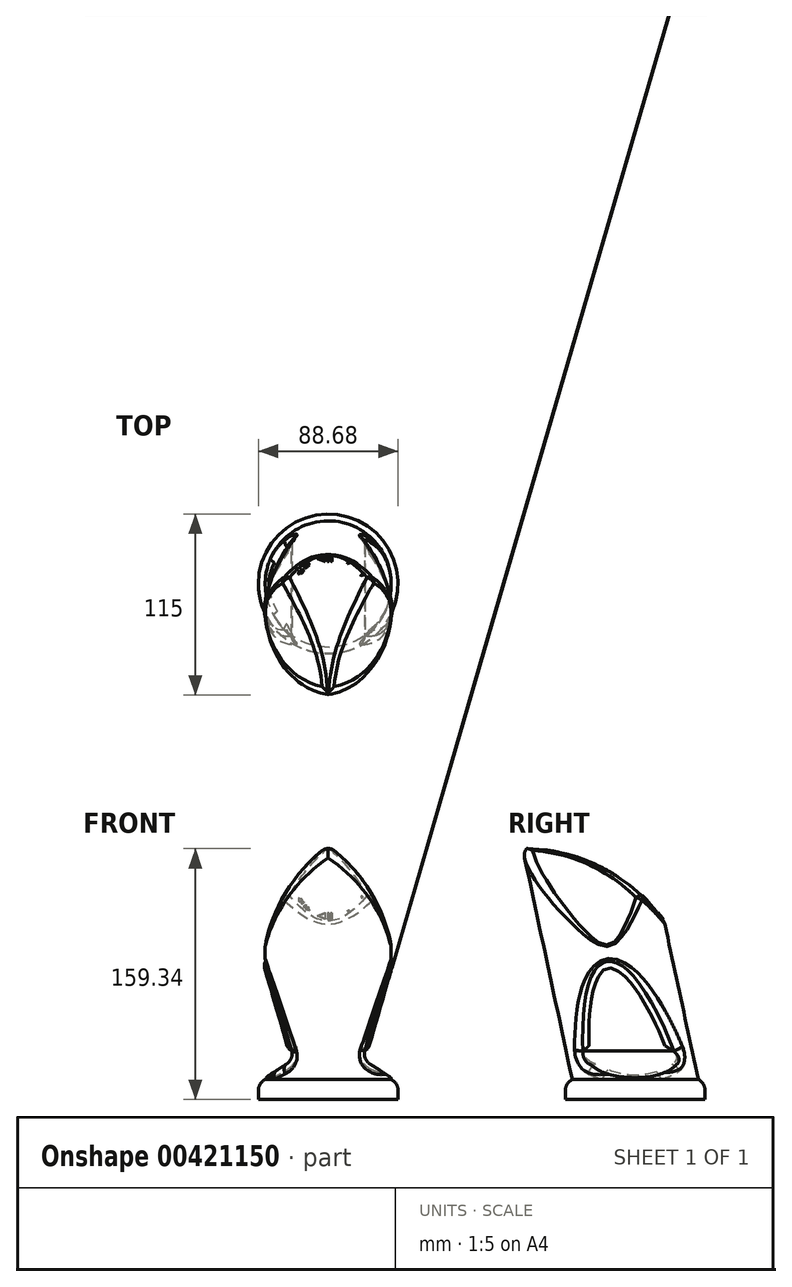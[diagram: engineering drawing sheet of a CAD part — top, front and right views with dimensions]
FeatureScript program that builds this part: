
annotation { "Feature Type Name" : "Feature", "Feature Type Description" : "" }
export const myFeature = defineFeature(function(context is Context, id is Id, definition is map)
    precondition{}
    {
        {
            var Q0;
            Q0=qCreatedBy(makeId("Top.planeOp"),FACE);
            var sketch = newSketch(context, id + "F0", { "sketchPlane" : qUnion([Q0])});
            skCircle(sketch, "E0", {"center": v(0, 0) * mm, "radius": 40 * mm});
            skSolve(sketch);
        }
        {
            var Q0;
            Q0=qCreatedBy(makeId("Right.planeOp"),FACE);
            var sketch = newSketch(context, id + "F1", { "sketchPlane" : qUnion([Q0])});
            skLineSegment(sketch, "E1", {"start": v(0, 0) * mm, "end": v(-31.49, 146.66) * mm});
            skSolve(sketch);
        }
        {
            var Q0;
            Q0=makeQuery(id+"F0.imprint","IMPRINT",FACE,{"disambiguationData":[TD([[makeQuery(id+"F0.imprint","IMPRINT",EDGE,{"derivedFrom":sQuery(id+"F0.wireOp",EDGE,"E0")}),1.0]])]});
            var Q1;
            Q1=sQuery(id+"F1.wireOp",EDGE,"E1");
            sweep(context, id + "F2", {"profiles" : qUnion([Q0]), "path" : qUnion([Q1])});
        }
        {
            var Q0;
            Q0=qCreatedBy(makeId("Right.planeOp"),FACE);
            var sketch = newSketch(context, id + "F3", { "sketchPlane" : qUnion([Q0])});
            skLineSegment(sketch, "E2", {"start": v(-70.9, 146.66) * mm, "end": v(9.55, 146.66) * mm});
            skArc(sketch, "E3", {"start": v(20.93, 96.2) * mm, "mid": v(-18.51, 133.21) * mm, "end": v(-70.9, 146.66) * mm});
            skLineSegment(sketch, "E4", {"start": v(9.55, 146.66) * mm, "end": v(20.93, 96.2) * mm});
            skSolve(sketch);
        }
        {
            var Q0;
            Q0=makeQuery(id+"F3.imprint","IMPRINT",FACE,{"disambiguationData":[TD([[makeQuery(id+"F3.imprint","IMPRINT",EDGE,{"derivedFrom":sQuery(id+"F3.wireOp",EDGE,"E2")}),-1.0]])]});
            extrude(context, id + "F4", {"entities" : qUnion([Q0]), "operationType" : NewBodyOperationType.REMOVE, "endBound" : BoundingType.SYMMETRIC, "depth" : 203.2 * mm});
        }
        {
            var Q0;
            Q0=makeQuery(id+"F2.opSweep","CAP_FACE",FACE,{"disambiguationData":[OSD([sQuery(id+"F0.wireOp",EDGE,"E0"),sQuery(id+"F1.wireOp",VERTEX,"E1.start")])],"isStart":true});
            var sketch = newSketch(context, id + "F5", { "sketchPlane" : qUnion([Q0])});
            skCircle(sketch, "E5", {"center": v(0, 0) * mm, "radius": 44.34 * mm});
            skSolve(sketch);
        }
        {
            var Q0;
            Q0 = qSketchRegion(id + "F5", true);
            extrude(context, id + "F6", {"entities" : qUnion([Q0]), "operationType" : NewBodyOperationType.ADD, "depth" : 12.7 * mm});
        }
        {
            var Q0;
            Q0=makeQuery(id+"F6.opExtrude","CAP_EDGE",EDGE,{"disambiguationData":[OSD([sQuery(id+"F5.wireOp",EDGE,"E5")])],"isStart":true});
            fillet(context, id + "F7", {"entities" : qUnion([Q0]), "radius" : 7.62 * mm, "tangentPropagation" : true, "allowEdgeOverflow" : false});
        }
        {
            var Q0;
            Q0=qCreatedBy(makeId("Front.planeOp"),FACE);
            var sketch = newSketch(context, id + "F8", { "sketchPlane" : qUnion([Q0])});
            skArc(sketch, "E6", {"start": v(41.27, 75.87) * mm, "mid": v(28.39, 116.5) * mm, "end": v(0, 148.3) * mm});
            skArc(sketch, "E7.MirrorCS", {"start": v(-41.27, 75.87) * mm, "mid": v(-28.39, 116.5) * mm, "end": v(0, 148.3) * mm});
            skLineSegment(sketch, "E8", {"start": v(41.27, 75.87) * mm, "end": v(43.39, 150.57) * mm});
            skLineSegment(sketch, "E9", {"start": v(43.39, 150.57) * mm, "end": v(-43.82, 150.57) * mm});
            skLineSegment(sketch, "E10", {"start": v(-43.82, 150.57) * mm, "end": v(-41.27, 75.87) * mm});
            skSolve(sketch);
        }
        {
            var Q0;
            Q0=makeQuery(id+"F8.imprint","IMPRINT",FACE,{"disambiguationData":[TD([[makeQuery(id+"F8.imprint","IMPRINT",EDGE,{"derivedFrom":sQuery(id+"F8.wireOp",EDGE,"E6")}),-1.0]])]});
            extrude(context, id + "F9", {"entities" : qUnion([Q0]), "operationType" : NewBodyOperationType.REMOVE, "endBound" : BoundingType.SYMMETRIC, "depth" : 177.8 * mm});
        }
        {
            var Q0;
            Q0=makeQuery(id+"F9.boolean.opBoolean","COPY",FACE,{"derivedFrom":makeQuery(id+"F9.opExtrude","SWEPT_FACE",FACE,{"disambiguationData":[OSD([sQuery(id+"F8.wireOp",EDGE,"E7.MirrorCS")])]})});
            var Q1;
            Q1=makeQuery(id+"F4.boolean.opBoolean","COPY",FACE,{"derivedFrom":makeQuery(id+"F4.opExtrude","SWEPT_FACE",FACE,{"disambiguationData":[OSD([sQuery(id+"F3.wireOp",EDGE,"E3")])]})});
            var Q2;
            Q2=makeQuery(id+"F9.boolean.opBoolean","COPY",FACE,{"derivedFrom":makeQuery(id+"F9.opExtrude","SWEPT_FACE",FACE,{"disambiguationData":[OSD([sQuery(id+"F8.wireOp",EDGE,"E6")])]})});
            fillet(context, id + "F10", {"entities" : qUnion([Q0, Q1, Q2]), "radius" : 5.08 * mm, "tangentPropagation" : true, "allowEdgeOverflow" : false});
        }
        {
            var Q0;
            Q0=qCreatedBy(makeId("Front.planeOp"),FACE);
            var sketch = newSketch(context, id + "F11", { "sketchPlane" : qUnion([Q0])});
            skLineSegment(sketch, "E11", {"start": v(26.48, 9.8) * mm, "end": v(41.75, 0) * mm});
            skPoint(sketch, "E12.visualSharp", {"position": v(21.88, 12.74) * mm});
            skArc(sketch, "E12.filletArc", {"start": v(23.2, 18.04) * mm, "mid": v(23.51, 13.4) * mm, "end": v(26.48, 9.8) * mm});
            skLineSegment(sketch, "E13", {"start": v(23.2, 18.04) * mm, "end": v(41.32, 80.51) * mm});
            skLineSegment(sketch, "E14", {"start": v(41.32, 80.51) * mm, "end": v(41.75, 0) * mm});
            skLineSegment(sketch, "E15.MirrorCS", {"start": v(-23.2, 18.04) * mm, "end": v(-41.32, 80.51) * mm});
            skLineSegment(sketch, "E16.MirrorCS", {"start": v(-41.32, 80.51) * mm, "end": v(-41.75, 0) * mm});
            skArc(sketch, "E17.MirrorCS", {"start": v(-23.2, 18.04) * mm, "mid": v(-23.51, 13.4) * mm, "end": v(-26.48, 9.8) * mm});
            skLineSegment(sketch, "E18.MirrorCS", {"start": v(-26.48, 9.8) * mm, "end": v(-41.75, 0) * mm});
            skSolve(sketch);
        }
        {
            var Q0;
            Q0=makeQuery(id+"F11.imprint","IMPRINT",FACE,{"disambiguationData":[TD([[makeQuery(id+"F11.imprint","IMPRINT",EDGE,{"derivedFrom":sQuery(id+"F11.wireOp",EDGE,"E11")}),1.0]])]});
            var Q1;
            Q1=makeQuery(id+"F11.imprint","IMPRINT",FACE,{"disambiguationData":[TD([[makeQuery(id+"F11.imprint","IMPRINT",EDGE,{"derivedFrom":sQuery(id+"F11.wireOp",EDGE,"E15.MirrorCS")}),1.0]])]});
            extrude(context, id + "F12", {"entities" : qUnion([Q0, Q1]), "operationType" : NewBodyOperationType.REMOVE, "endBound" : BoundingType.SYMMETRIC, "oppositeDirection" : true, "depth" : 101.6 * mm});
        }
        {
            var Q0;
            Q0=makeQuery(id+"F12.boolean.opBoolean","COPY",FACE,{"derivedFrom":makeQuery(id+"F12.opExtrude","SWEPT_FACE",FACE,{"disambiguationData":[OSD([sQuery(id+"F11.wireOp",EDGE,"E15.MirrorCS")])]})});
            var Q1;
            Q1=makeQuery(id+"F12.boolean.opBoolean","COPY",FACE,{"derivedFrom":makeQuery(id+"F12.opExtrude","SWEPT_FACE",FACE,{"disambiguationData":[OSD([sQuery(id+"F11.wireOp",EDGE,"E18.MirrorCS")])]})});
            var Q2;
            Q2=makeQuery(id+"F12.boolean.opBoolean","COPY",FACE,{"derivedFrom":makeQuery(id+"F12.opExtrude","SWEPT_FACE",FACE,{"disambiguationData":[OSD([sQuery(id+"F11.wireOp",EDGE,"E13")])]})});
            fillet(context, id + "F13", {"entities" : qUnion([Q0, Q1, Q2]), "radius" : 6.35 * mm, "tangentPropagation" : true, "allowEdgeOverflow" : false});
        }
        {
            var Q0;
            {var subQ0=makeQuery(id+"F4.opExtrude","SWEPT_FACE",FACE,{"disambiguationData":[OSD([sQuery(id+"F3.wireOp",EDGE,"E3")])]});Q0=makeQuery(id+"F10.opFillet","BLEND_EDGE",EDGE,{"blendedFrom":[makeQuery(id+"F4.boolean.opBoolean","INTERSECT",EDGE,{"derivedFrom":[makeQuery(id+"F2.opSweep","SWEPT_FACE",FACE,{"disambiguationData":[OSD([sQuery(id+"F0.wireOp",EDGE,"E0"),sQuery(id+"F1.wireOp",EDGE,"E1")])]}),subQ0]}),makeQuery(id+"F4.boolean.opBoolean","COPY",FACE,{"derivedFrom":subQ0})],"blendedInto":[makeQuery(id+"F4.boolean.opBoolean","COPY",FACE,{"derivedFrom":subQ0})]});}
            cPoint(context, id + "F14", {"entities" : qUnion([Q0]), "parameter" : 0.5});
        }
        {
            var Q0;
            {var subQ0=makeQuery(id+"F4.opExtrude","SWEPT_FACE",FACE,{"disambiguationData":[OSD([sQuery(id+"F3.wireOp",EDGE,"E3")])]});var subQ1=makeQuery(id+"F4.boolean.opBoolean","COPY",FACE,{"derivedFrom":subQ0});var subQ2=makeQuery(id+"F9.opExtrude","SWEPT_FACE",FACE,{"disambiguationData":[OSD([sQuery(id+"F8.wireOp",EDGE,"E6")])]});var subQ3=makeQuery(id+"F2.opSweep","SWEPT_FACE",FACE,{"disambiguationData":[OSD([sQuery(id+"F0.wireOp",EDGE,"E0"),sQuery(id+"F1.wireOp",EDGE,"E1")])]});Q0=makeQuery(id+"F10.opFillet","BLEND_VERTEX",VERTEX,{"blendedFrom":[makeQuery(id+"F9.boolean.opBoolean","INTERSECT",VERTEX,{"derivedFrom":[subQ1,subQ3,subQ2]}),makeQuery(id+"F4.boolean.opBoolean","INTERSECT",EDGE,{"derivedFrom":[subQ3,subQ0]}),makeQuery(id+"F9.boolean.opBoolean","INTERSECT",EDGE,{"derivedFrom":[subQ1,subQ2]}),subQ1],"blendedInto":[subQ1]});}
            var Q1;
            {var subQ0=makeQuery(id+"F4.opExtrude","SWEPT_FACE",FACE,{"disambiguationData":[OSD([sQuery(id+"F3.wireOp",EDGE,"E3")])]});var subQ1=makeQuery(id+"F4.boolean.opBoolean","COPY",FACE,{"derivedFrom":subQ0});var subQ2=makeQuery(id+"F9.opExtrude","SWEPT_FACE",FACE,{"disambiguationData":[OSD([sQuery(id+"F8.wireOp",EDGE,"E7.MirrorCS")])]});var subQ3=makeQuery(id+"F2.opSweep","SWEPT_FACE",FACE,{"disambiguationData":[OSD([sQuery(id+"F0.wireOp",EDGE,"E0"),sQuery(id+"F1.wireOp",EDGE,"E1")])]});Q1=makeQuery(id+"F10.opFillet","BLEND_VERTEX",VERTEX,{"blendedFrom":[makeQuery(id+"F9.boolean.opBoolean","INTERSECT",VERTEX,{"derivedFrom":[subQ1,subQ3,subQ2]}),makeQuery(id+"F4.boolean.opBoolean","INTERSECT",EDGE,{"derivedFrom":[subQ3,subQ0]}),makeQuery(id+"F9.boolean.opBoolean","INTERSECT",EDGE,{"derivedFrom":[subQ1,subQ2]}),subQ1],"blendedInto":[subQ1]});}
            var Q2;
            Q2 = qCreatedBy(id + "F14" ,VERTEX);
            cPlane(context, id + "F15", {"entities" : qUnion([Q0, Q1, Q2]), "cplaneType" : CPlaneType.THREE_POINT, "offset" : 163.58 * mm, "width" : 152.4 * mm, "height" : 152.4 * mm});
        }
        {
            var Q0;
            Q0=qCreatedBy(id+"F15.planeOp",FACE);
            var sketch = newSketch(context, id + "F16", { "sketchPlane" : qUnion([Q0])});
            skLineSegment(sketch, "E19", {"start": v(2.1, 70.8) * mm, "end": v(2.1, 65.8) * mm});
            skLineSegment(sketch, "E20", {"start": v(2.1, 65.8) * mm, "end": v(6.79, 68.3) * mm});
            skLineSegment(sketch, "E21", {"start": v(6.79, 68.3) * mm, "end": v(2.1, 70.8) * mm});
            skLineSegment(sketch, "E22.bottom", {"start": v(0.38, 70.8) * mm, "end": v(-0.61, 70.8) * mm});
            skLineSegment(sketch, "E22.top", {"start": v(0.38, 65.8) * mm, "end": v(-0.61, 65.8) * mm});
            skLineSegment(sketch, "E22.left", {"start": v(0.38, 70.8) * mm, "end": v(0.38, 65.8) * mm});
            skLineSegment(sketch, "E22.right", {"start": v(-0.61, 70.8) * mm, "end": v(-0.61, 65.8) * mm});
            skLineSegment(sketch, "E23.bottom", {"start": v(-2.33, 70.8) * mm, "end": v(-1.43, 70.8) * mm});
            skLineSegment(sketch, "E23.top", {"start": v(-2.33, 65.8) * mm, "end": v(-1.43, 65.8) * mm});
            skLineSegment(sketch, "E23.left", {"start": v(-2.33, 70.8) * mm, "end": v(-2.33, 65.8) * mm});
            skLineSegment(sketch, "E23.right", {"start": v(-1.43, 70.8) * mm, "end": v(-1.43, 65.8) * mm});
            skFitSpline(sketch, "E24.0", {"points": [v(-22.72, 86.68) * mm, v(-22.05, 85.48) * mm, v(-20.64, 83.11) * mm, v(-18.36, 79.71) * mm, v(-15.9, 76.47) * mm, v(-13.89, 74.2) * mm, v(-12.47, 72.76) * mm, v(-11.5, 71.82) * mm, v(-10.24, 70.72) * mm, v(-8.7, 69.53) * mm, v(-7.07, 68.47) * mm, v(-5.4, 67.58) * mm, v(-3.61, 66.9) * mm, v(-1.83, 66.47) * mm, v(-0.33, 66.35) * mm, v(0.89, 66.4) * mm, v(2.09, 66.54) * mm, v(3.28, 66.81) * mm, v(4.45, 67.22) * mm, v(5.62, 67.7) * mm, v(7.02, 68.44) * mm, v(8.64, 69.49) * mm, v(10.19, 70.68) * mm, v(11.68, 71.99) * mm, v(13.61, 73.88) * mm, v(15.85, 76.41) * mm, v(18.34, 79.68) * mm, v(20.64, 83.11) * mm, v(22.05, 85.48) * mm, v(22.72, 86.68) * mm]});
            skLineSegment(sketch, "E25", {"start": v(-20.58, 83.09) * mm, "end": v(-16.54, 83.09) * mm});
            skLineSegment(sketch, "E26", {"start": v(-19.28, 81.1) * mm, "end": v(-14.86, 81.1) * mm});
            skLineSegment(sketch, "E27", {"start": v(-17.5, 78.6) * mm, "end": v(-14.86, 78.6) * mm});
            skLineSegment(sketch, "E28", {"start": v(-16.39, 77.16) * mm, "end": v(-13.65, 77.16) * mm});
            skLineSegment(sketch, "E29", {"start": v(-14.67, 75.1) * mm, "end": v(-12.58, 75.1) * mm});
            skLineSegment(sketch, "E30", {"start": v(-13.41, 73.72) * mm, "end": v(-11.3, 73.72) * mm});
            skFitSpline(sketch, "E31.trimOffspring", {"points": [v(-22.72, 86.68) * mm, v(-22.05, 85.48) * mm, v(-20.64, 83.11) * mm, v(-18.36, 79.71) * mm, v(-15.9, 76.47) * mm, v(-13.89, 74.2) * mm, v(-12.47, 72.76) * mm, v(-11.5, 71.82) * mm, v(-10.24, 70.72) * mm, v(-8.7, 69.53) * mm, v(-7.07, 68.47) * mm, v(-5.4, 67.58) * mm, v(-3.61, 66.9) * mm, v(-1.83, 66.47) * mm, v(-0.33, 66.35) * mm, v(0.89, 66.4) * mm, v(2.09, 66.54) * mm, v(3.28, 66.81) * mm, v(4.45, 67.22) * mm, v(5.62, 67.7) * mm, v(7.02, 68.44) * mm, v(8.64, 69.49) * mm, v(10.19, 70.68) * mm, v(11.68, 71.99) * mm, v(13.61, 73.88) * mm, v(15.85, 76.41) * mm, v(18.34, 79.68) * mm, v(20.64, 83.11) * mm, v(22.05, 85.48) * mm, v(22.72, 86.68) * mm]});
            skFitSpline(sketch, "E32.trimOffspring", {"points": [v(-22.72, 86.68) * mm, v(-22.05, 85.48) * mm, v(-20.64, 83.11) * mm, v(-18.36, 79.71) * mm, v(-15.9, 76.47) * mm, v(-13.89, 74.2) * mm, v(-12.47, 72.76) * mm, v(-11.5, 71.82) * mm, v(-10.24, 70.72) * mm, v(-8.7, 69.53) * mm, v(-7.07, 68.47) * mm, v(-5.4, 67.58) * mm, v(-3.61, 66.9) * mm, v(-1.83, 66.47) * mm, v(-0.33, 66.35) * mm, v(0.89, 66.4) * mm, v(2.09, 66.54) * mm, v(3.28, 66.81) * mm, v(4.45, 67.22) * mm, v(5.62, 67.7) * mm, v(7.02, 68.44) * mm, v(8.64, 69.49) * mm, v(10.19, 70.68) * mm, v(11.68, 71.99) * mm, v(13.61, 73.88) * mm, v(15.85, 76.41) * mm, v(18.34, 79.68) * mm, v(20.64, 83.11) * mm, v(22.05, 85.48) * mm, v(22.72, 86.68) * mm]});
            skLineSegment(sketch, "E33", {"start": v(-16.54, 83.09) * mm, "end": v(-14.86, 81.1) * mm});
            skLineSegment(sketch, "E34", {"start": v(-14.86, 78.6) * mm, "end": v(-13.65, 77.16) * mm});
            skLineSegment(sketch, "E35", {"start": v(-12.58, 75.1) * mm, "end": v(-11.3, 73.72) * mm});
            skPoint(sketch, "E36.orphan", {"position": v(-13.65, 78.6) * mm});
            skPoint(sketch, "E37.orphan", {"position": v(-10.49, 75.1) * mm});
            skPoint(sketch, "E38.orphan", {"position": v(-9.2, 73.72) * mm});
            skLineSegment(sketch, "E39", {"start": v(-21.47, 84.78) * mm, "end": v(-21.08, 84.78) * mm});
            skLineSegment(sketch, "E40", {"start": v(-21.08, 84.78) * mm, "end": v(-21.08, 84.46) * mm});
            skLineSegment(sketch, "E41", {"start": v(-21.08, 84.46) * mm, "end": v(-20.75, 84.46) * mm});
            skLineSegment(sketch, "E42", {"start": v(-20.75, 84.46) * mm, "end": v(-20.75, 83.99) * mm});
            skLineSegment(sketch, "E43", {"start": v(-20.75, 83.99) * mm, "end": v(-21.08, 83.99) * mm});
            skLineSegment(sketch, "E44", {"start": v(-21.08, 83.99) * mm, "end": v(-21.08, 83.67) * mm});
            skLineSegment(sketch, "E45", {"start": v(-21.08, 83.67) * mm, "end": v(-21.47, 83.67) * mm});
            skLineSegment(sketch, "E46", {"start": v(-21.47, 83.67) * mm, "end": v(-21.47, 83.99) * mm});
            skLineSegment(sketch, "E47", {"start": v(-21.47, 83.99) * mm, "end": v(-21.8, 83.99) * mm});
            skLineSegment(sketch, "E48", {"start": v(-21.8, 83.99) * mm, "end": v(-21.8, 84.46) * mm});
            skLineSegment(sketch, "E49", {"start": v(-21.8, 84.46) * mm, "end": v(-21.47, 84.46) * mm});
            skLineSegment(sketch, "E50", {"start": v(-21.47, 84.46) * mm, "end": v(-21.47, 84.78) * mm});
            skLineSegment(sketch, "E51", {"start": v(-13.53, 72.6) * mm, "end": v(-12.4, 72.6) * mm});
            skLineSegment(sketch, "E52", {"start": v(-12.4, 72.6) * mm, "end": v(-12.4, 72.23) * mm});
            skLineSegment(sketch, "E53", {"start": v(-12.4, 72.23) * mm, "end": v(-13.53, 72.23) * mm});
            skLineSegment(sketch, "E54", {"start": v(-13.53, 72.23) * mm, "end": v(-13.53, 72.6) * mm});
            skLineSegment(sketch, "E55", {"start": v(12.37, 75.69) * mm, "end": v(14.32, 74.03) * mm});
            skLineSegment(sketch, "E56", {"start": v(14.32, 74.03) * mm, "end": v(11.98, 73.08) * mm});
            skLineSegment(sketch, "E57", {"start": v(11.98, 73.08) * mm, "end": v(12.37, 75.69) * mm});
            skLineSegment(sketch, "E58", {"start": v(13.95, 77.62) * mm, "end": v(15.58, 76.24) * mm});
            skLineSegment(sketch, "E59", {"start": v(15.58, 76.24) * mm, "end": v(13.35, 75.05) * mm});
            skLineSegment(sketch, "E60", {"start": v(13.35, 75.05) * mm, "end": v(13.95, 77.62) * mm});
            skLineSegment(sketch, "E61", {"start": v(18.63, 80.52) * mm, "end": v(16.67, 82.18) * mm});
            skLineSegment(sketch, "E62", {"start": v(16.67, 82.18) * mm, "end": v(19.01, 83.13) * mm});
            skLineSegment(sketch, "E63", {"start": v(19.01, 83.13) * mm, "end": v(18.63, 80.52) * mm});
            skLineSegment(sketch, "E64", {"start": v(17.05, 78.58) * mm, "end": v(15.42, 79.97) * mm});
            skLineSegment(sketch, "E65", {"start": v(15.42, 79.97) * mm, "end": v(17.65, 81.16) * mm});
            skLineSegment(sketch, "E66", {"start": v(17.65, 81.16) * mm, "end": v(17.05, 78.58) * mm});
            skSolve(sketch);
        }
        {
            var Q0;
            Q0 = qSketchRegion(id + "F16", true);
            extrude(context, id + "F17", {"entities" : qUnion([Q0]), "depth" : 0.69 * mm});
        }
        {
            var Q0;
            Q0=makeQuery(id+"F17.opExtrude","CAP_FACE",FACE,{"disambiguationData":[OSD([sQuery(id+"F16.wireOp",EDGE,"E39"),sQuery(id+"F16.wireOp",EDGE,"E40"),sQuery(id+"F16.wireOp",EDGE,"E41"),sQuery(id+"F16.wireOp",EDGE,"E42"),sQuery(id+"F16.wireOp",EDGE,"E43"),sQuery(id+"F16.wireOp",EDGE,"E44"),sQuery(id+"F16.wireOp",EDGE,"E45"),sQuery(id+"F16.wireOp",EDGE,"E46"),sQuery(id+"F16.wireOp",EDGE,"E47"),sQuery(id+"F16.wireOp",EDGE,"E48"),sQuery(id+"F16.wireOp",EDGE,"E49"),sQuery(id+"F16.wireOp",EDGE,"E50")])],"isStart":false});
            var Q1;
            Q1=makeQuery(id+"F17.opExtrude","CAP_FACE",FACE,{"disambiguationData":[OSD([sQuery(id+"F16.wireOp",EDGE,"E24.0"),sQuery(id+"F16.wireOp",EDGE,"E25"),sQuery(id+"F16.wireOp",EDGE,"E26"),sQuery(id+"F16.wireOp",EDGE,"E33")])],"isStart":false});
            var Q2;
            Q2=makeQuery(id+"F17.opExtrude","CAP_FACE",FACE,{"disambiguationData":[OSD([sQuery(id+"F16.wireOp",EDGE,"E27"),sQuery(id+"F16.wireOp",EDGE,"E28"),sQuery(id+"F16.wireOp",EDGE,"E31.trimOffspring"),sQuery(id+"F16.wireOp",EDGE,"E34")])],"isStart":false});
            var Q3;
            Q3=makeQuery(id+"F17.opExtrude","CAP_FACE",FACE,{"disambiguationData":[OSD([sQuery(id+"F16.wireOp",EDGE,"E29"),sQuery(id+"F16.wireOp",EDGE,"E30"),sQuery(id+"F16.wireOp",EDGE,"E32.trimOffspring"),sQuery(id+"F16.wireOp",EDGE,"E35")])],"isStart":false});
            var Q4;
            Q4=makeQuery(id+"F17.opExtrude","CAP_FACE",FACE,{"disambiguationData":[OSD([sQuery(id+"F16.wireOp",EDGE,"E51"),sQuery(id+"F16.wireOp",EDGE,"E52"),sQuery(id+"F16.wireOp",EDGE,"E53"),sQuery(id+"F16.wireOp",EDGE,"E54")])],"isStart":false});
            var Q5;
            Q5=makeQuery(id+"F17.opExtrude","CAP_FACE",FACE,{"disambiguationData":[OSD([sQuery(id+"F16.wireOp",EDGE,"E23.bottom"),sQuery(id+"F16.wireOp",EDGE,"E23.top"),sQuery(id+"F16.wireOp",EDGE,"E23.left"),sQuery(id+"F16.wireOp",EDGE,"E23.right")])],"isStart":false});
            var Q6;
            Q6=makeQuery(id+"F17.opExtrude","CAP_FACE",FACE,{"disambiguationData":[OSD([sQuery(id+"F16.wireOp",EDGE,"E22.bottom"),sQuery(id+"F16.wireOp",EDGE,"E22.top"),sQuery(id+"F16.wireOp",EDGE,"E22.left"),sQuery(id+"F16.wireOp",EDGE,"E22.right")])],"isStart":false});
            var Q7;
            Q7=makeQuery(id+"F17.opExtrude","CAP_FACE",FACE,{"disambiguationData":[OSD([sQuery(id+"F16.wireOp",EDGE,"E19"),sQuery(id+"F16.wireOp",EDGE,"E20"),sQuery(id+"F16.wireOp",EDGE,"E21")])],"isStart":false});
            var Q8;
            Q8=makeQuery(id+"F17.opExtrude","CAP_FACE",FACE,{"disambiguationData":[OSD([sQuery(id+"F16.wireOp",EDGE,"E61"),sQuery(id+"F16.wireOp",EDGE,"E62"),sQuery(id+"F16.wireOp",EDGE,"E63")])],"isStart":false});
            var Q9;
            Q9=makeQuery(id+"F17.opExtrude","CAP_FACE",FACE,{"disambiguationData":[OSD([sQuery(id+"F16.wireOp",EDGE,"E64"),sQuery(id+"F16.wireOp",EDGE,"E65"),sQuery(id+"F16.wireOp",EDGE,"E66")])],"isStart":false});
            var Q10;
            Q10=makeQuery(id+"F17.opExtrude","CAP_FACE",FACE,{"disambiguationData":[OSD([sQuery(id+"F16.wireOp",EDGE,"E58"),sQuery(id+"F16.wireOp",EDGE,"E59"),sQuery(id+"F16.wireOp",EDGE,"E60")])],"isStart":false});
            var Q11;
            Q11=makeQuery(id+"F17.opExtrude","CAP_FACE",FACE,{"disambiguationData":[OSD([sQuery(id+"F16.wireOp",EDGE,"E55"),sQuery(id+"F16.wireOp",EDGE,"E56"),sQuery(id+"F16.wireOp",EDGE,"E57")])],"isStart":false});
            fillet(context, id + "F18", {"entities" : qUnion([Q0, Q1, Q2, Q3, Q4, Q5, Q6, Q7, Q8, Q9, Q10, Q11]), "radius" : 0.18 * mm, "tangentPropagation" : true, "allowEdgeOverflow" : false});
        }
        {
            var Q0;
            Q0=makeQuery(id+"F12.boolean.opBoolean","COPY",FACE,{"derivedFrom":makeQuery(id+"F12.opExtrude","SWEPT_FACE",FACE,{"disambiguationData":[OSD([sQuery(id+"F11.wireOp",EDGE,"E13")])]})});
            var sketch = newSketch(context, id + "F19", { "sketchPlane" : qUnion([Q0])});
            skLineSegment(sketch, "E67.0.0", {"start": v(-33.12, 23.97) * mm, "end": v(24.54, 23.97) * mm});
            skFitSpline(sketch, "E67.0.1", {"points": [v(24.54, 23.97) * mm, v(23.53, 26.7) * mm, v(21.43, 32.13) * mm, v(18.06, 40.17) * mm, v(14.43, 48.07) * mm, v(11.13, 54.52) * mm, v(8.3, 59.58) * mm, v(6.04, 63.32) * mm, v(3.65, 66.98) * mm, v(1.07, 70.56) * mm, v(-1.23, 73.4) * mm, v(-3.18, 75.56) * mm, v(-4.72, 77.11) * mm, v(-6.08, 78.34) * mm, v(-7.22, 79.27) * mm, v(-8.4, 80.17) * mm, v(-9.93, 81.19) * mm, v(-11.56, 82.03) * mm, v(-12.95, 82.58) * mm, v(-14.01, 82.9) * mm, v(-14.92, 83.07) * mm, v(-15.65, 83.16) * mm, v(-16.4, 83.2) * mm, v(-17.32, 83.18) * mm, v(-18.23, 83.04) * mm, v(-18.95, 82.86) * mm, v(-19.66, 82.63) * mm, v(-20.5, 82.26) * mm, v(-21.3, 81.8) * mm, v(-21.92, 81.38) * mm, v(-22.5, 80.93) * mm, v(-23.2, 80.32) * mm, v(-24.2, 79.26) * mm, v(-25.1, 78.1) * mm, v(-25.9, 76.88) * mm, v(-26.65, 75.6) * mm, v(-27.48, 73.96) * mm, v(-28.33, 71.92) * mm, v(-29.08, 69.84) * mm, v(-29.95, 67.03) * mm, v(-30.83, 63.48) * mm, v(-31.64, 59.15) * mm, v(-32.26, 54.78) * mm, v(-32.72, 50.4) * mm, v(-33.04, 46) * mm, v(-33.31, 40.13) * mm, v(-33.4, 32.78) * mm, v(-33.24, 26.9) * mm, v(-33.12, 23.97) * mm]});
            skSolve(sketch);
        }
        {
            var Q0;
            Q0 = qSketchRegion(id + "F19", true);
            extrude(context, id + "F20", {"entities" : qUnion([Q0]), "depth" : 1.78 * mm});
        }
        {
            var Q0;
            Q0=makeQuery(id+"F20.opExtrude","CAP_FACE",FACE,{"disambiguationData":[OSD([sQuery(id+"F19.wireOp",EDGE,"E67.0.0"),sQuery(id+"F19.wireOp",EDGE,"E67.0.1")])],"isStart":false});
            fillet(context, id + "F21", {"entities" : qUnion([Q0]), "radius" : 5.08 * mm, "tangentPropagation" : true, "allowEdgeOverflow" : false});
        }
        {
            var Q0;
            Q0=makeQuery(id+"F12.boolean.opBoolean","COPY",FACE,{"derivedFrom":makeQuery(id+"F12.opExtrude","SWEPT_FACE",FACE,{"disambiguationData":[OSD([sQuery(id+"F11.wireOp",EDGE,"E15.MirrorCS")])]})});
            var sketch = newSketch(context, id + "F22", { "sketchPlane" : qUnion([Q0])});
            skFitSpline(sketch, "E68.0", {"points": [v(33.12, 23.97) * mm, v(33.24, 26.87) * mm, v(33.36, 31.24) * mm, v(33.35, 37.05) * mm, v(33.25, 41.4) * mm, v(33.06, 45.74) * mm, v(32.75, 50.06) * mm, v(32.3, 54.38) * mm, v(31.72, 58.67) * mm, v(31.07, 62.24) * mm, v(30.43, 65.08) * mm, v(29.88, 67.2) * mm, v(29.25, 69.31) * mm, v(28.54, 71.38) * mm, v(27.72, 73.41) * mm, v(26.93, 75.06) * mm, v(26.23, 76.34) * mm, v(25.65, 77.28) * mm, v(25.02, 78.2) * mm, v(24.35, 79.06) * mm, v(23.63, 79.89) * mm, v(22.84, 80.65) * mm, v(21.97, 81.36) * mm, v(21.06, 81.96) * mm, v(20.25, 82.38) * mm, v(19.56, 82.66) * mm, v(18.86, 82.9) * mm, v(17.96, 83.1) * mm, v(16.86, 83.2) * mm, v(15.74, 83.18) * mm, v(14.65, 83.03) * mm, v(13.58, 82.78) * mm, v(12.52, 82.42) * mm, v(11.5, 81.99) * mm, v(10.52, 81.49) * mm, v(9.57, 80.93) * mm, v(8.64, 80.33) * mm, v(7.74, 79.68) * mm, v(6.59, 78.77) * mm, v(5.2, 77.57) * mm, v(3.63, 76.03) * mm, v(2.12, 74.4) * mm, v(0.69, 72.73) * mm, v(-1.15, 70.44) * mm, v(-3.31, 67.47) * mm, v(-5.74, 63.8) * mm, v(-8.04, 60.02) * mm, v(-10.2, 56.18) * mm, v(-12.27, 52.29) * mm, v(-14.9, 47.02) * mm, v(-17.98, 40.35) * mm, v(-21.4, 32.22) * mm, v(-23.52, 26.73) * mm, v(-24.54, 23.97) * mm]});
            skLineSegment(sketch, "E69.0.0", {"start": v(-24.54, 23.97) * mm, "end": v(33.12, 23.97) * mm});
            skFitSpline(sketch, "E69.0.1", {"points": [v(33.12, 23.97) * mm, v(33.24, 26.87) * mm, v(33.36, 31.24) * mm, v(33.35, 37.05) * mm, v(33.25, 41.4) * mm, v(33.06, 45.74) * mm, v(32.75, 50.06) * mm, v(32.3, 54.38) * mm, v(31.72, 58.67) * mm, v(31.07, 62.24) * mm, v(30.43, 65.08) * mm, v(29.88, 67.2) * mm, v(29.25, 69.31) * mm, v(28.54, 71.38) * mm, v(27.72, 73.41) * mm, v(26.93, 75.06) * mm, v(26.23, 76.34) * mm, v(25.65, 77.28) * mm, v(25.02, 78.2) * mm, v(24.35, 79.06) * mm, v(23.63, 79.89) * mm, v(22.84, 80.65) * mm, v(21.97, 81.36) * mm, v(21.06, 81.96) * mm, v(20.25, 82.38) * mm, v(19.56, 82.66) * mm, v(18.86, 82.9) * mm, v(17.96, 83.1) * mm, v(16.86, 83.2) * mm, v(15.74, 83.18) * mm, v(14.65, 83.03) * mm, v(13.58, 82.78) * mm, v(12.52, 82.42) * mm, v(11.5, 81.99) * mm, v(10.52, 81.49) * mm, v(9.57, 80.93) * mm, v(8.64, 80.33) * mm, v(7.74, 79.68) * mm, v(6.59, 78.77) * mm, v(5.2, 77.57) * mm, v(3.63, 76.03) * mm, v(2.12, 74.4) * mm, v(0.69, 72.73) * mm, v(-1.15, 70.44) * mm, v(-3.31, 67.47) * mm, v(-5.74, 63.8) * mm, v(-8.04, 60.02) * mm, v(-10.2, 56.18) * mm, v(-12.27, 52.29) * mm, v(-14.9, 47.02) * mm, v(-17.98, 40.35) * mm, v(-21.4, 32.22) * mm, v(-23.52, 26.73) * mm, v(-24.54, 23.97) * mm]});
            skSolve(sketch);
        }
        {
            var Q0;
            Q0 = qSketchRegion(id + "F22", true);
            extrude(context, id + "F23", {"entities" : qUnion([Q0]), "depth" : 1.78 * mm});
        }
        {
            var Q0;
            Q0=makeQuery(id+"F23.opExtrude","CAP_FACE",FACE,{"disambiguationData":[OSD([sQuery(id+"F22.wireOp",EDGE,"E69.0.0"),sQuery(id+"F22.wireOp",EDGE,"E69.0.1")])],"isStart":false});
            fillet(context, id + "F24", {"entities" : qUnion([Q0]), "radius" : 5.08 * mm, "tangentPropagation" : true, "allowEdgeOverflow" : false});
        }
    });
